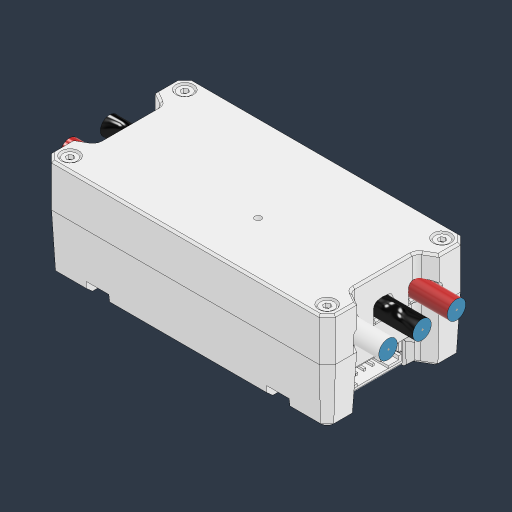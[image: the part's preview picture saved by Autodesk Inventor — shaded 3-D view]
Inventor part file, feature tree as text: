
AUTODESK INVENTOR PART (.ipt)
format: ipt  version: 2024.3 (Build 283343000, 343)  size: 2,231,296 bytes
history: native  units: in
note: dims shown in document units (in); Inventor stores cm internally (conversion verified against a paired STEP export)
features: other x18, sketch x4
ambient origin geometry x8: Origin, YZ Plane, XZ Plane, XY Plane, X Axis, Y Axis, Z Axis, Center Point
bodies: Solid1 (feature_tree), Solid2 (feature_tree), Solid3 (feature_tree), Solid4 (feature_tree), Solid5 (feature_tree), Solid6 (feature_tree), Solid7 (feature_tree), Solid8 (feature_tree), Solid9 (feature_tree), Solid10 (feature_tree), Solid11 (feature_tree), Solid12 (feature_tree), Solid13 (feature_tree), Solid14 (feature_tree), Solid15 (feature_tree), Solid16 (feature_tree), Solid17 (feature_tree), Solid18 (feature_tree)
feature tree (22):
  sketch  "Sketch1"
  sketch  "Sketch2"
  sketch  "Sketch3"
  sketch  "Sketch4"
  parser-record x1  (decoder bookkeeping rows leaked as tree rows — omitted from the tree; the rows remain in map.json)
  other  "NONE:1"
  other  "NONE:2"
  other  "NONE:3"
  other  "NONE:4"
  other  "NONE:5"
  other  "NONE:6"
  other  "NONE:7"
  other  "NONE:8"
  other  "NONE:9"
  other  "NONE:10"
  other  "NONE:11"
  other  "NONE:12"
  other  "Cut-Extrude1[1]"
  other  "Cut-Extrude1[2]"
  other  "Cut-Extrude1[3]"
  other  "Cut-Extrude1[4]"
  other  "Cut-Extrude1[5]"
